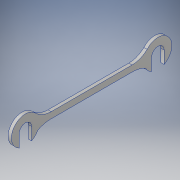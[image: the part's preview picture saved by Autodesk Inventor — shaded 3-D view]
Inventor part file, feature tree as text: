
AUTODESK INVENTOR PART (.ipt)
format: ipt  version: 2018 (Build 220112000, 112)  size: 120,320 bytes
history: native  units: in
note: dims shown in document units (in); Inventor stores cm internally (conversion verified against a paired STEP export)
features: extrude x1, sketch x1
ambient origin geometry x8: Origin, YZ Plane, XZ Plane, XY Plane, X Axis, Y Axis, Z Axis, Center Point
bodies: Body1 (feature_tree)
feature tree (2):
  extrude  "Extrusion2"  Depth=0.077in
  sketch  "Sketch1"  dims[d0=0.173in d10=0.25in d11=0.077in d12=0.02in d13=0.0in]
